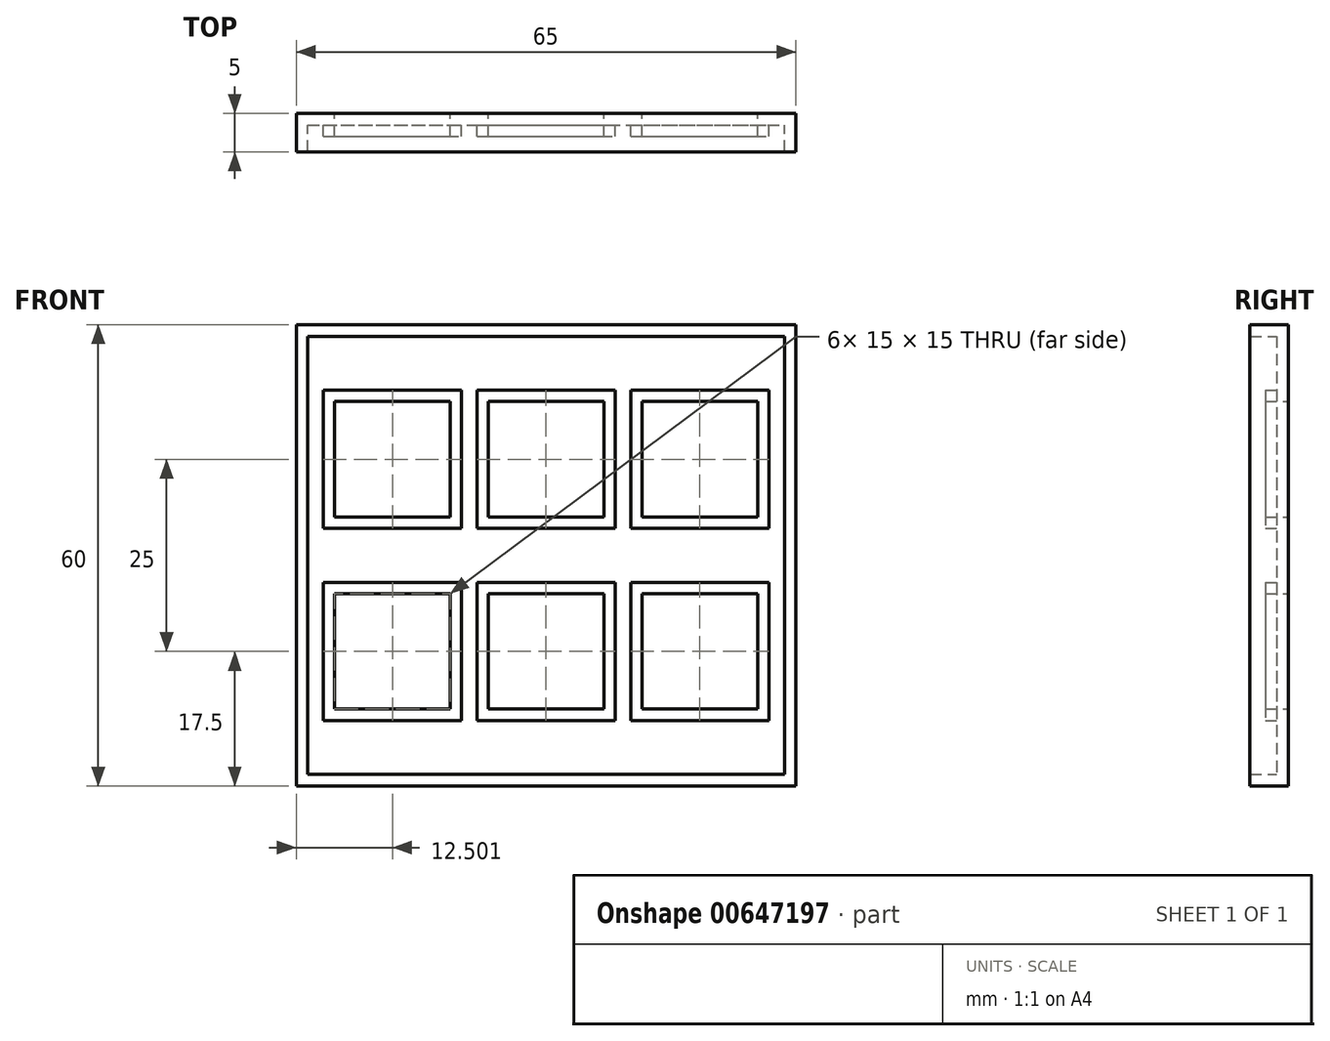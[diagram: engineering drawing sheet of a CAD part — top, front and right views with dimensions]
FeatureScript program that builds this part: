
annotation { "Feature Type Name" : "Feature", "Feature Type Description" : "" }
export const myFeature = defineFeature(function(context is Context, id is Id, definition is map)
    precondition{}
    {
        {
            var Q0;
            Q0=qCreatedBy(makeId("Front.planeOp"),FACE);
            var sketch = newSketch(context, id + "F0", { "sketchPlane" : qUnion([Q0])});
            skLineSegment(sketch, "E0.bottom", {"start": v(8.97, 50) * mm, "end": v(23.97, 50) * mm});
            skLineSegment(sketch, "E0.top", {"start": v(8.97, 35) * mm, "end": v(23.97, 35) * mm});
            skLineSegment(sketch, "E0.left", {"start": v(8.97, 50) * mm, "end": v(8.97, 35) * mm});
            skLineSegment(sketch, "E0.right", {"start": v(23.97, 50) * mm, "end": v(23.97, 35) * mm});
            skLineSegment(sketch, "E1.bottom", {"start": v(28.97, 50) * mm, "end": v(43.97, 50) * mm});
            skLineSegment(sketch, "E1.top", {"start": v(28.97, 35) * mm, "end": v(43.97, 35) * mm});
            skLineSegment(sketch, "E1.left", {"start": v(28.97, 50) * mm, "end": v(28.97, 35) * mm});
            skLineSegment(sketch, "E1.right", {"start": v(43.97, 50) * mm, "end": v(43.97, 35) * mm});
            skLineSegment(sketch, "E2.bottom", {"start": v(48.97, 50) * mm, "end": v(63.97, 50) * mm});
            skLineSegment(sketch, "E2.top", {"start": v(48.97, 35) * mm, "end": v(63.97, 35) * mm});
            skLineSegment(sketch, "E2.left", {"start": v(48.97, 50) * mm, "end": v(48.97, 35) * mm});
            skLineSegment(sketch, "E2.right", {"start": v(63.97, 50) * mm, "end": v(63.97, 35) * mm});
            skLineSegment(sketch, "E3.bottom", {"start": v(8.97, 25) * mm, "end": v(23.97, 25) * mm});
            skLineSegment(sketch, "E3.top", {"start": v(8.97, 10) * mm, "end": v(23.97, 10) * mm});
            skLineSegment(sketch, "E3.left", {"start": v(8.97, 25) * mm, "end": v(8.97, 10) * mm});
            skLineSegment(sketch, "E3.right", {"start": v(23.97, 25) * mm, "end": v(23.97, 10) * mm});
            skLineSegment(sketch, "E4.bottom", {"start": v(28.97, 25) * mm, "end": v(43.97, 25) * mm});
            skLineSegment(sketch, "E4.top", {"start": v(28.97, 10) * mm, "end": v(43.97, 10) * mm});
            skLineSegment(sketch, "E4.left", {"start": v(28.97, 25) * mm, "end": v(28.97, 10) * mm});
            skLineSegment(sketch, "E4.right", {"start": v(43.97, 25) * mm, "end": v(43.97, 10) * mm});
            skLineSegment(sketch, "E5.bottom", {"start": v(48.97, 25) * mm, "end": v(63.97, 25) * mm});
            skLineSegment(sketch, "E5.top", {"start": v(48.97, 10) * mm, "end": v(63.97, 10) * mm});
            skLineSegment(sketch, "E5.left", {"start": v(48.97, 25) * mm, "end": v(48.97, 10) * mm});
            skLineSegment(sketch, "E5.right", {"start": v(63.97, 25) * mm, "end": v(63.97, 10) * mm});
            skLineSegment(sketch, "E6.bottom", {"start": v(3.97, 60) * mm, "end": v(68.97, 60) * mm});
            skLineSegment(sketch, "E6.top", {"start": v(3.97, 0) * mm, "end": v(68.97, 0) * mm});
            skLineSegment(sketch, "E6.left", {"start": v(3.97, 60) * mm, "end": v(3.97, 0) * mm});
            skLineSegment(sketch, "E6.right", {"start": v(68.97, 60) * mm, "end": v(68.97, 0) * mm});
            skSolve(sketch);
        }
        {
            var Q0;
            Q0=makeQuery(id+"F0.imprint","IMPRINT",FACE,{"disambiguationData":[TD([[makeQuery(id+"F0.imprint","IMPRINT",EDGE,{"derivedFrom":sQuery(id+"F0.wireOp",EDGE,"E0.bottom")}),1.0]])]});
            var Q1;
            Q1=sQuery(id+"F0.wireOp",EDGE,"E2.bottom");
            var Q2;
            Q2=sQuery(id+"F0.wireOp",EDGE,"E2.left");
            var Q3;
            Q3=sQuery(id+"F0.wireOp",EDGE,"E2.top");
            var Q4;
            Q4=sQuery(id+"F0.wireOp",EDGE,"E2.right");
            var Q5;
            Q5=sQuery(id+"F0.wireOp",EDGE,"E1.bottom");
            var Q6;
            Q6=sQuery(id+"F0.wireOp",EDGE,"E1.top");
            var Q7;
            Q7=sQuery(id+"F0.wireOp",EDGE,"E1.right");
            var Q8;
            Q8=sQuery(id+"F0.wireOp",EDGE,"E1.left");
            var Q9;
            Q9=sQuery(id+"F0.wireOp",EDGE,"E0.right");
            var Q10;
            Q10=sQuery(id+"F0.wireOp",EDGE,"E0.bottom");
            var Q11;
            Q11=sQuery(id+"F0.wireOp",EDGE,"E0.left");
            var Q12;
            Q12=sQuery(id+"F0.wireOp",EDGE,"E0.top");
            var Q13;
            Q13=sQuery(id+"F0.wireOp",EDGE,"E3.bottom");
            var Q14;
            Q14=sQuery(id+"F0.wireOp",EDGE,"E3.top");
            var Q15;
            Q15=sQuery(id+"F0.wireOp",EDGE,"E3.left");
            var Q16;
            Q16=sQuery(id+"F0.wireOp",EDGE,"E3.right");
            var Q17;
            Q17=sQuery(id+"F0.wireOp",EDGE,"E4.left");
            var Q18;
            Q18=sQuery(id+"F0.wireOp",EDGE,"E4.bottom");
            var Q19;
            Q19=sQuery(id+"F0.wireOp",EDGE,"E4.top");
            var Q20;
            Q20=sQuery(id+"F0.wireOp",EDGE,"E4.right");
            var Q21;
            Q21=sQuery(id+"F0.wireOp",EDGE,"E5.bottom");
            var Q22;
            Q22=sQuery(id+"F0.wireOp",EDGE,"E5.left");
            var Q23;
            Q23=sQuery(id+"F0.wireOp",EDGE,"E5.top");
            var Q24;
            Q24=sQuery(id+"F0.wireOp",EDGE,"E5.right");
            var Q25;
            Q25=sQuery(id+"F0.wireOp",EDGE,"E6.right");
            var Q26;
            Q26=sQuery(id+"F0.wireOp",EDGE,"E6.bottom");
            var Q27;
            Q27=sQuery(id+"F0.wireOp",EDGE,"E6.left");
            var Q28;
            Q28=sQuery(id+"F0.wireOp",EDGE,"E6.top");
            extrude(context, id + "F1", {"entities" : qUnion([Q0]), "surfaceEntities" : qUnion([Q1, Q2, Q3, Q4, Q5, Q6, Q7, Q8, Q9, Q10, Q11, Q12, Q13, Q14, Q15, Q16, Q17, Q18, Q19, Q20, Q21, Q22, Q23, Q24, Q25, Q26, Q27, Q28]), "depth" : 5 * mm, "offsetDistance" : 25 * mm});
        }
        {
            var Q0;
            Q0=makeQuery(id+"F1.opExtrude","CAP_FACE",FACE,{"disambiguationData":[OSD([sQuery(id+"F0.wireOp",EDGE,"E0.bottom"),sQuery(id+"F0.wireOp",EDGE,"E0.top"),sQuery(id+"F0.wireOp",EDGE,"E0.left"),sQuery(id+"F0.wireOp",EDGE,"E0.right"),sQuery(id+"F0.wireOp",EDGE,"E1.bottom"),sQuery(id+"F0.wireOp",EDGE,"E1.top"),sQuery(id+"F0.wireOp",EDGE,"E1.left"),sQuery(id+"F0.wireOp",EDGE,"E1.right"),sQuery(id+"F0.wireOp",EDGE,"E2.bottom"),sQuery(id+"F0.wireOp",EDGE,"E2.top"),sQuery(id+"F0.wireOp",EDGE,"E2.left"),sQuery(id+"F0.wireOp",EDGE,"E2.right"),sQuery(id+"F0.wireOp",EDGE,"E3.bottom"),sQuery(id+"F0.wireOp",EDGE,"E3.top"),sQuery(id+"F0.wireOp",EDGE,"E3.left"),sQuery(id+"F0.wireOp",EDGE,"E3.right"),sQuery(id+"F0.wireOp",EDGE,"E4.bottom"),sQuery(id+"F0.wireOp",EDGE,"E4.top"),sQuery(id+"F0.wireOp",EDGE,"E4.left"),sQuery(id+"F0.wireOp",EDGE,"E4.right"),sQuery(id+"F0.wireOp",EDGE,"E5.bottom"),sQuery(id+"F0.wireOp",EDGE,"E5.top"),sQuery(id+"F0.wireOp",EDGE,"E5.left"),sQuery(id+"F0.wireOp",EDGE,"E5.right"),sQuery(id+"F0.wireOp",EDGE,"E6.bottom"),sQuery(id+"F0.wireOp",EDGE,"E6.top"),sQuery(id+"F0.wireOp",EDGE,"E6.left"),sQuery(id+"F0.wireOp",EDGE,"E6.right")])],"isStart":false});
            var Q1;
            Q1=makeQuery(id+"F1.opExtrude","SWEPT_BODY",BODY,{"disambiguationData":[OSD([sQuery(id+"F0.wireOp",EDGE,"E0.bottom"),sQuery(id+"F0.wireOp",EDGE,"E0.top"),sQuery(id+"F0.wireOp",EDGE,"E0.left"),sQuery(id+"F0.wireOp",EDGE,"E0.right"),sQuery(id+"F0.wireOp",EDGE,"E1.bottom"),sQuery(id+"F0.wireOp",EDGE,"E1.top"),sQuery(id+"F0.wireOp",EDGE,"E1.left"),sQuery(id+"F0.wireOp",EDGE,"E1.right"),sQuery(id+"F0.wireOp",EDGE,"E2.bottom"),sQuery(id+"F0.wireOp",EDGE,"E2.top"),sQuery(id+"F0.wireOp",EDGE,"E2.left"),sQuery(id+"F0.wireOp",EDGE,"E2.right"),sQuery(id+"F0.wireOp",EDGE,"E3.bottom"),sQuery(id+"F0.wireOp",EDGE,"E3.top"),sQuery(id+"F0.wireOp",EDGE,"E3.left"),sQuery(id+"F0.wireOp",EDGE,"E3.right"),sQuery(id+"F0.wireOp",EDGE,"E4.bottom"),sQuery(id+"F0.wireOp",EDGE,"E4.top"),sQuery(id+"F0.wireOp",EDGE,"E4.left"),sQuery(id+"F0.wireOp",EDGE,"E4.right"),sQuery(id+"F0.wireOp",EDGE,"E5.bottom"),sQuery(id+"F0.wireOp",EDGE,"E5.top"),sQuery(id+"F0.wireOp",EDGE,"E5.left"),sQuery(id+"F0.wireOp",EDGE,"E5.right"),sQuery(id+"F0.wireOp",EDGE,"E6.bottom"),sQuery(id+"F0.wireOp",EDGE,"E6.top"),sQuery(id+"F0.wireOp",EDGE,"E6.left"),sQuery(id+"F0.wireOp",EDGE,"E6.right")])]});
            shell(context, id + "F2", {"entities" : qUnion([Q0]), "parts" : qUnion([Q1]), "thickness" : 1.5 * mm});
        }
        {
            var Q0;
            {var subQ0=sQuery(id+"F0.wireOp",EDGE,"E6.right");var subQ1=sQuery(id+"F0.wireOp",EDGE,"E6.left");var subQ2=sQuery(id+"F0.wireOp",EDGE,"E6.top");var subQ3=sQuery(id+"F0.wireOp",EDGE,"E6.bottom");var subQ4=sQuery(id+"F0.wireOp",EDGE,"E5.right");var subQ5=sQuery(id+"F0.wireOp",EDGE,"E5.left");var subQ6=sQuery(id+"F0.wireOp",EDGE,"E5.top");var subQ7=sQuery(id+"F0.wireOp",EDGE,"E5.bottom");var subQ8=sQuery(id+"F0.wireOp",EDGE,"E4.right");var subQ9=sQuery(id+"F0.wireOp",EDGE,"E4.left");var subQ10=sQuery(id+"F0.wireOp",EDGE,"E4.top");var subQ11=sQuery(id+"F0.wireOp",EDGE,"E4.bottom");var subQ12=sQuery(id+"F0.wireOp",EDGE,"E3.right");var subQ13=sQuery(id+"F0.wireOp",EDGE,"E3.left");var subQ14=sQuery(id+"F0.wireOp",EDGE,"E3.top");var subQ15=sQuery(id+"F0.wireOp",EDGE,"E3.bottom");var subQ16=sQuery(id+"F0.wireOp",EDGE,"E2.right");var subQ17=sQuery(id+"F0.wireOp",EDGE,"E2.left");var subQ18=sQuery(id+"F0.wireOp",EDGE,"E2.top");var subQ19=sQuery(id+"F0.wireOp",EDGE,"E2.bottom");var subQ20=sQuery(id+"F0.wireOp",EDGE,"E1.right");var subQ21=sQuery(id+"F0.wireOp",EDGE,"E1.left");var subQ22=sQuery(id+"F0.wireOp",EDGE,"E1.top");var subQ23=sQuery(id+"F0.wireOp",EDGE,"E1.bottom");var subQ24=sQuery(id+"F0.wireOp",EDGE,"E0.right");var subQ25=sQuery(id+"F0.wireOp",EDGE,"E0.left");var subQ26=sQuery(id+"F0.wireOp",EDGE,"E0.top");var subQ27=sQuery(id+"F0.wireOp",EDGE,"E0.bottom");Q0=makeQuery(id+"F2.opShell","OFFSET_FACE",FACE,{"disambiguationData":[OSD([subQ27,subQ26,subQ25,subQ24,subQ23,subQ22,subQ21,subQ20,subQ19,subQ18,subQ17,subQ16,subQ15,subQ14,subQ13,subQ12,subQ11,subQ10,subQ9,subQ8,subQ7,subQ6,subQ5,subQ4,subQ3,subQ2,subQ1,subQ0]),TDD([makeQuery(id+"F1.opExtrude","CAP_FACE",FACE,{"disambiguationData":[OSD([subQ27,subQ26,subQ25,subQ24,subQ23,subQ22,subQ21,subQ20,subQ19,subQ18,subQ17,subQ16,subQ15,subQ14,subQ13,subQ12,subQ11,subQ10,subQ9,subQ8,subQ7,subQ6,subQ5,subQ4,subQ3,subQ2,subQ1,subQ0])],"isStart":false})]),OD(3.0)]});}
            var Q1;
            {var subQ0=sQuery(id+"F0.wireOp",EDGE,"E6.right");var subQ1=sQuery(id+"F0.wireOp",EDGE,"E6.left");var subQ2=sQuery(id+"F0.wireOp",EDGE,"E6.top");var subQ3=sQuery(id+"F0.wireOp",EDGE,"E6.bottom");var subQ4=sQuery(id+"F0.wireOp",EDGE,"E5.right");var subQ5=sQuery(id+"F0.wireOp",EDGE,"E5.left");var subQ6=sQuery(id+"F0.wireOp",EDGE,"E5.top");var subQ7=sQuery(id+"F0.wireOp",EDGE,"E5.bottom");var subQ8=sQuery(id+"F0.wireOp",EDGE,"E4.right");var subQ9=sQuery(id+"F0.wireOp",EDGE,"E4.left");var subQ10=sQuery(id+"F0.wireOp",EDGE,"E4.top");var subQ11=sQuery(id+"F0.wireOp",EDGE,"E4.bottom");var subQ12=sQuery(id+"F0.wireOp",EDGE,"E3.right");var subQ13=sQuery(id+"F0.wireOp",EDGE,"E3.left");var subQ14=sQuery(id+"F0.wireOp",EDGE,"E3.top");var subQ15=sQuery(id+"F0.wireOp",EDGE,"E3.bottom");var subQ16=sQuery(id+"F0.wireOp",EDGE,"E2.right");var subQ17=sQuery(id+"F0.wireOp",EDGE,"E2.left");var subQ18=sQuery(id+"F0.wireOp",EDGE,"E2.top");var subQ19=sQuery(id+"F0.wireOp",EDGE,"E2.bottom");var subQ20=sQuery(id+"F0.wireOp",EDGE,"E1.right");var subQ21=sQuery(id+"F0.wireOp",EDGE,"E1.left");var subQ22=sQuery(id+"F0.wireOp",EDGE,"E1.top");var subQ23=sQuery(id+"F0.wireOp",EDGE,"E1.bottom");var subQ24=sQuery(id+"F0.wireOp",EDGE,"E0.right");var subQ25=sQuery(id+"F0.wireOp",EDGE,"E0.left");var subQ26=sQuery(id+"F0.wireOp",EDGE,"E0.top");var subQ27=sQuery(id+"F0.wireOp",EDGE,"E0.bottom");Q1=makeQuery(id+"F2.opShell","OFFSET_FACE",FACE,{"disambiguationData":[OSD([subQ27,subQ26,subQ25,subQ24,subQ23,subQ22,subQ21,subQ20,subQ19,subQ18,subQ17,subQ16,subQ15,subQ14,subQ13,subQ12,subQ11,subQ10,subQ9,subQ8,subQ7,subQ6,subQ5,subQ4,subQ3,subQ2,subQ1,subQ0]),TDD([makeQuery(id+"F1.opExtrude","CAP_FACE",FACE,{"disambiguationData":[OSD([subQ27,subQ26,subQ25,subQ24,subQ23,subQ22,subQ21,subQ20,subQ19,subQ18,subQ17,subQ16,subQ15,subQ14,subQ13,subQ12,subQ11,subQ10,subQ9,subQ8,subQ7,subQ6,subQ5,subQ4,subQ3,subQ2,subQ1,subQ0])],"isStart":false})]),OD(4.0)]});}
            var Q2;
            {var subQ0=sQuery(id+"F0.wireOp",EDGE,"E6.right");var subQ1=sQuery(id+"F0.wireOp",EDGE,"E6.left");var subQ2=sQuery(id+"F0.wireOp",EDGE,"E6.top");var subQ3=sQuery(id+"F0.wireOp",EDGE,"E6.bottom");var subQ4=sQuery(id+"F0.wireOp",EDGE,"E5.right");var subQ5=sQuery(id+"F0.wireOp",EDGE,"E5.left");var subQ6=sQuery(id+"F0.wireOp",EDGE,"E5.top");var subQ7=sQuery(id+"F0.wireOp",EDGE,"E5.bottom");var subQ8=sQuery(id+"F0.wireOp",EDGE,"E4.right");var subQ9=sQuery(id+"F0.wireOp",EDGE,"E4.left");var subQ10=sQuery(id+"F0.wireOp",EDGE,"E4.top");var subQ11=sQuery(id+"F0.wireOp",EDGE,"E4.bottom");var subQ12=sQuery(id+"F0.wireOp",EDGE,"E3.right");var subQ13=sQuery(id+"F0.wireOp",EDGE,"E3.left");var subQ14=sQuery(id+"F0.wireOp",EDGE,"E3.top");var subQ15=sQuery(id+"F0.wireOp",EDGE,"E3.bottom");var subQ16=sQuery(id+"F0.wireOp",EDGE,"E2.right");var subQ17=sQuery(id+"F0.wireOp",EDGE,"E2.left");var subQ18=sQuery(id+"F0.wireOp",EDGE,"E2.top");var subQ19=sQuery(id+"F0.wireOp",EDGE,"E2.bottom");var subQ20=sQuery(id+"F0.wireOp",EDGE,"E1.right");var subQ21=sQuery(id+"F0.wireOp",EDGE,"E1.left");var subQ22=sQuery(id+"F0.wireOp",EDGE,"E1.top");var subQ23=sQuery(id+"F0.wireOp",EDGE,"E1.bottom");var subQ24=sQuery(id+"F0.wireOp",EDGE,"E0.right");var subQ25=sQuery(id+"F0.wireOp",EDGE,"E0.left");var subQ26=sQuery(id+"F0.wireOp",EDGE,"E0.top");var subQ27=sQuery(id+"F0.wireOp",EDGE,"E0.bottom");Q2=makeQuery(id+"F2.opShell","OFFSET_FACE",FACE,{"disambiguationData":[OSD([subQ27,subQ26,subQ25,subQ24,subQ23,subQ22,subQ21,subQ20,subQ19,subQ18,subQ17,subQ16,subQ15,subQ14,subQ13,subQ12,subQ11,subQ10,subQ9,subQ8,subQ7,subQ6,subQ5,subQ4,subQ3,subQ2,subQ1,subQ0]),TDD([makeQuery(id+"F1.opExtrude","CAP_FACE",FACE,{"disambiguationData":[OSD([subQ27,subQ26,subQ25,subQ24,subQ23,subQ22,subQ21,subQ20,subQ19,subQ18,subQ17,subQ16,subQ15,subQ14,subQ13,subQ12,subQ11,subQ10,subQ9,subQ8,subQ7,subQ6,subQ5,subQ4,subQ3,subQ2,subQ1,subQ0])],"isStart":false})]),OD(5.0)]});}
            var Q3;
            {var subQ0=sQuery(id+"F0.wireOp",EDGE,"E6.right");var subQ1=sQuery(id+"F0.wireOp",EDGE,"E6.left");var subQ2=sQuery(id+"F0.wireOp",EDGE,"E6.top");var subQ3=sQuery(id+"F0.wireOp",EDGE,"E6.bottom");var subQ4=sQuery(id+"F0.wireOp",EDGE,"E5.right");var subQ5=sQuery(id+"F0.wireOp",EDGE,"E5.left");var subQ6=sQuery(id+"F0.wireOp",EDGE,"E5.top");var subQ7=sQuery(id+"F0.wireOp",EDGE,"E5.bottom");var subQ8=sQuery(id+"F0.wireOp",EDGE,"E4.right");var subQ9=sQuery(id+"F0.wireOp",EDGE,"E4.left");var subQ10=sQuery(id+"F0.wireOp",EDGE,"E4.top");var subQ11=sQuery(id+"F0.wireOp",EDGE,"E4.bottom");var subQ12=sQuery(id+"F0.wireOp",EDGE,"E3.right");var subQ13=sQuery(id+"F0.wireOp",EDGE,"E3.left");var subQ14=sQuery(id+"F0.wireOp",EDGE,"E3.top");var subQ15=sQuery(id+"F0.wireOp",EDGE,"E3.bottom");var subQ16=sQuery(id+"F0.wireOp",EDGE,"E2.right");var subQ17=sQuery(id+"F0.wireOp",EDGE,"E2.left");var subQ18=sQuery(id+"F0.wireOp",EDGE,"E2.top");var subQ19=sQuery(id+"F0.wireOp",EDGE,"E2.bottom");var subQ20=sQuery(id+"F0.wireOp",EDGE,"E1.right");var subQ21=sQuery(id+"F0.wireOp",EDGE,"E1.left");var subQ22=sQuery(id+"F0.wireOp",EDGE,"E1.top");var subQ23=sQuery(id+"F0.wireOp",EDGE,"E1.bottom");var subQ24=sQuery(id+"F0.wireOp",EDGE,"E0.right");var subQ25=sQuery(id+"F0.wireOp",EDGE,"E0.left");var subQ26=sQuery(id+"F0.wireOp",EDGE,"E0.top");var subQ27=sQuery(id+"F0.wireOp",EDGE,"E0.bottom");Q3=makeQuery(id+"F2.opShell","OFFSET_FACE",FACE,{"disambiguationData":[OSD([subQ27,subQ26,subQ25,subQ24,subQ23,subQ22,subQ21,subQ20,subQ19,subQ18,subQ17,subQ16,subQ15,subQ14,subQ13,subQ12,subQ11,subQ10,subQ9,subQ8,subQ7,subQ6,subQ5,subQ4,subQ3,subQ2,subQ1,subQ0]),TDD([makeQuery(id+"F1.opExtrude","CAP_FACE",FACE,{"disambiguationData":[OSD([subQ27,subQ26,subQ25,subQ24,subQ23,subQ22,subQ21,subQ20,subQ19,subQ18,subQ17,subQ16,subQ15,subQ14,subQ13,subQ12,subQ11,subQ10,subQ9,subQ8,subQ7,subQ6,subQ5,subQ4,subQ3,subQ2,subQ1,subQ0])],"isStart":false})]),OD(2.0)]});}
            var Q4;
            {var subQ0=sQuery(id+"F0.wireOp",EDGE,"E6.right");var subQ1=sQuery(id+"F0.wireOp",EDGE,"E6.left");var subQ2=sQuery(id+"F0.wireOp",EDGE,"E6.top");var subQ3=sQuery(id+"F0.wireOp",EDGE,"E6.bottom");var subQ4=sQuery(id+"F0.wireOp",EDGE,"E5.right");var subQ5=sQuery(id+"F0.wireOp",EDGE,"E5.left");var subQ6=sQuery(id+"F0.wireOp",EDGE,"E5.top");var subQ7=sQuery(id+"F0.wireOp",EDGE,"E5.bottom");var subQ8=sQuery(id+"F0.wireOp",EDGE,"E4.right");var subQ9=sQuery(id+"F0.wireOp",EDGE,"E4.left");var subQ10=sQuery(id+"F0.wireOp",EDGE,"E4.top");var subQ11=sQuery(id+"F0.wireOp",EDGE,"E4.bottom");var subQ12=sQuery(id+"F0.wireOp",EDGE,"E3.right");var subQ13=sQuery(id+"F0.wireOp",EDGE,"E3.left");var subQ14=sQuery(id+"F0.wireOp",EDGE,"E3.top");var subQ15=sQuery(id+"F0.wireOp",EDGE,"E3.bottom");var subQ16=sQuery(id+"F0.wireOp",EDGE,"E2.right");var subQ17=sQuery(id+"F0.wireOp",EDGE,"E2.left");var subQ18=sQuery(id+"F0.wireOp",EDGE,"E2.top");var subQ19=sQuery(id+"F0.wireOp",EDGE,"E2.bottom");var subQ20=sQuery(id+"F0.wireOp",EDGE,"E1.right");var subQ21=sQuery(id+"F0.wireOp",EDGE,"E1.left");var subQ22=sQuery(id+"F0.wireOp",EDGE,"E1.top");var subQ23=sQuery(id+"F0.wireOp",EDGE,"E1.bottom");var subQ24=sQuery(id+"F0.wireOp",EDGE,"E0.right");var subQ25=sQuery(id+"F0.wireOp",EDGE,"E0.left");var subQ26=sQuery(id+"F0.wireOp",EDGE,"E0.top");var subQ27=sQuery(id+"F0.wireOp",EDGE,"E0.bottom");Q4=makeQuery(id+"F2.opShell","OFFSET_FACE",FACE,{"disambiguationData":[OSD([subQ27,subQ26,subQ25,subQ24,subQ23,subQ22,subQ21,subQ20,subQ19,subQ18,subQ17,subQ16,subQ15,subQ14,subQ13,subQ12,subQ11,subQ10,subQ9,subQ8,subQ7,subQ6,subQ5,subQ4,subQ3,subQ2,subQ1,subQ0]),TDD([makeQuery(id+"F1.opExtrude","CAP_FACE",FACE,{"disambiguationData":[OSD([subQ27,subQ26,subQ25,subQ24,subQ23,subQ22,subQ21,subQ20,subQ19,subQ18,subQ17,subQ16,subQ15,subQ14,subQ13,subQ12,subQ11,subQ10,subQ9,subQ8,subQ7,subQ6,subQ5,subQ4,subQ3,subQ2,subQ1,subQ0])],"isStart":false})]),OD(1.0)]});}
            var Q5;
            {var subQ0=sQuery(id+"F0.wireOp",EDGE,"E6.right");var subQ1=sQuery(id+"F0.wireOp",EDGE,"E6.left");var subQ2=sQuery(id+"F0.wireOp",EDGE,"E6.top");var subQ3=sQuery(id+"F0.wireOp",EDGE,"E6.bottom");var subQ4=sQuery(id+"F0.wireOp",EDGE,"E5.right");var subQ5=sQuery(id+"F0.wireOp",EDGE,"E5.left");var subQ6=sQuery(id+"F0.wireOp",EDGE,"E5.top");var subQ7=sQuery(id+"F0.wireOp",EDGE,"E5.bottom");var subQ8=sQuery(id+"F0.wireOp",EDGE,"E4.right");var subQ9=sQuery(id+"F0.wireOp",EDGE,"E4.left");var subQ10=sQuery(id+"F0.wireOp",EDGE,"E4.top");var subQ11=sQuery(id+"F0.wireOp",EDGE,"E4.bottom");var subQ12=sQuery(id+"F0.wireOp",EDGE,"E3.right");var subQ13=sQuery(id+"F0.wireOp",EDGE,"E3.left");var subQ14=sQuery(id+"F0.wireOp",EDGE,"E3.top");var subQ15=sQuery(id+"F0.wireOp",EDGE,"E3.bottom");var subQ16=sQuery(id+"F0.wireOp",EDGE,"E2.right");var subQ17=sQuery(id+"F0.wireOp",EDGE,"E2.left");var subQ18=sQuery(id+"F0.wireOp",EDGE,"E2.top");var subQ19=sQuery(id+"F0.wireOp",EDGE,"E2.bottom");var subQ20=sQuery(id+"F0.wireOp",EDGE,"E1.right");var subQ21=sQuery(id+"F0.wireOp",EDGE,"E1.left");var subQ22=sQuery(id+"F0.wireOp",EDGE,"E1.top");var subQ23=sQuery(id+"F0.wireOp",EDGE,"E1.bottom");var subQ24=sQuery(id+"F0.wireOp",EDGE,"E0.right");var subQ25=sQuery(id+"F0.wireOp",EDGE,"E0.left");var subQ26=sQuery(id+"F0.wireOp",EDGE,"E0.top");var subQ27=sQuery(id+"F0.wireOp",EDGE,"E0.bottom");Q5=makeQuery(id+"F2.opShell","OFFSET_FACE",FACE,{"disambiguationData":[OSD([subQ27,subQ26,subQ25,subQ24,subQ23,subQ22,subQ21,subQ20,subQ19,subQ18,subQ17,subQ16,subQ15,subQ14,subQ13,subQ12,subQ11,subQ10,subQ9,subQ8,subQ7,subQ6,subQ5,subQ4,subQ3,subQ2,subQ1,subQ0]),TDD([makeQuery(id+"F1.opExtrude","CAP_FACE",FACE,{"disambiguationData":[OSD([subQ27,subQ26,subQ25,subQ24,subQ23,subQ22,subQ21,subQ20,subQ19,subQ18,subQ17,subQ16,subQ15,subQ14,subQ13,subQ12,subQ11,subQ10,subQ9,subQ8,subQ7,subQ6,subQ5,subQ4,subQ3,subQ2,subQ1,subQ0])],"isStart":false})]),OD(0.0)]});}
            extrude(context, id + "F3", {"entities" : qUnion([Q0, Q1, Q2, Q3, Q4, Q5]), "operationType" : NewBodyOperationType.REMOVE, "oppositeDirection" : true, "depth" : 2 * mm, "offsetDistance" : 25 * mm});
        }
    });
